# Revit family: 95800038
name_source: partatom
category: Equipamento especial
revit_build: Autodesk Revit 2016 (Build: 20150220_1215(x64)
units: mm (PartAtom-declared; Revit-internal decimal feet)

## family parameters
Com base no plano de trabalho = Não
Compartilhado = Não
Corte com vazios quando carregados = Não
Cota do conector redondo = Utilizar diâmetro
Ponto de cálculo do ambiente = Não
Sempre na vertical = Sim
Tipo de parte = Normal

## types (2) — shared parameters
Classe de Construção = Classe I
Desenvolvedor = Factory Cursos & Desenvolvimento
Disjuntor termomagnético = 10 A
Fabricante = Tramontina
Filtors de Aluminio (lavável) = 2
Filtros de Carvão Ativado = 2
Frequência = 60 Hz
Grau de proteção = IPX0
Iluminação (2 x 1,0 W - 12 V ) = Lampadas Led - Cor 3200 K
Nivel de Ruido = 63 dB
Numero de Velocidades = 3
Peso Bruto = 25,40 kg
Peso liquido = 20,30 kg
Potência Elétrica = 190 W
Potência Motor = 185 W
Recorte do Movel para Instalação = 725 x 250
Site do desenvolvedor = www.factorycursos.com.br
URL = www.tramontina.com.br
Vazão Máxima = 630 m3/h

## per-type parameters (varying)
| type | Código de montagem | Descrição | Modelo | Tensão |
| Tramontina Coifa de Embutir - 95800/015 | 95800/015 | 95800/015 | Coifa de Embutir - Incasso 75 | 127 V |
| Tramontina Coifa de Embutir Incasso Black 95800038 | 95800038 | 95800038 | Coifa de Embutir - Incasso 75 Black | 220 V |
